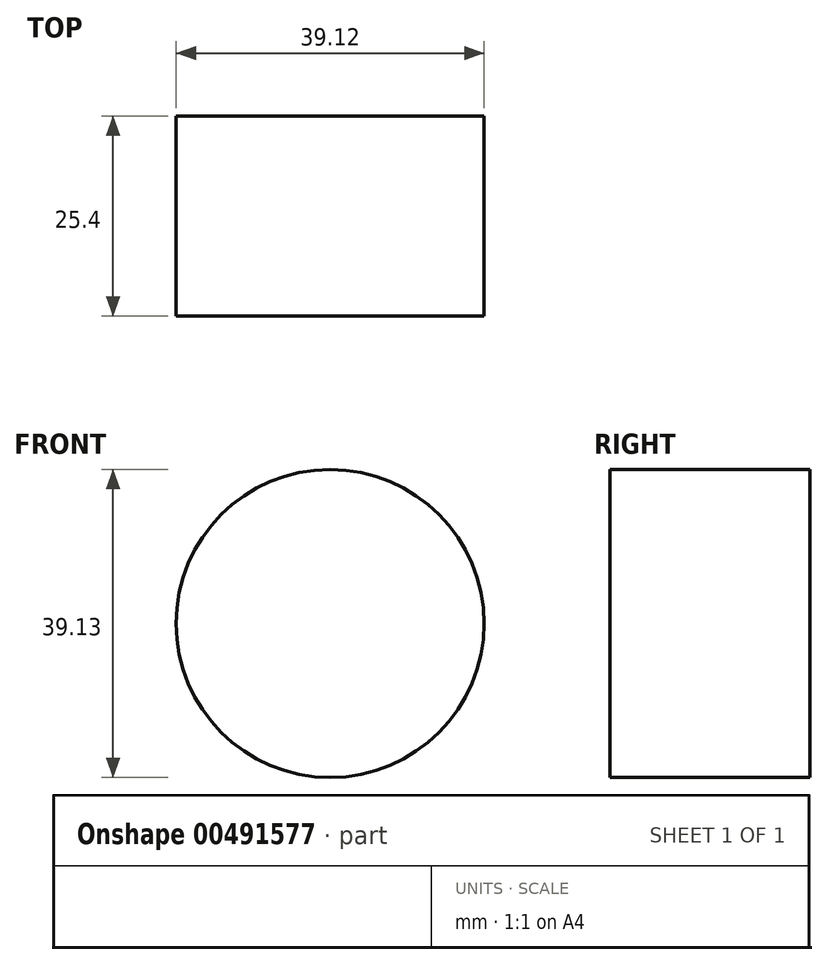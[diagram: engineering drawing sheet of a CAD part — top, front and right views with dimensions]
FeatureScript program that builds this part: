
annotation { "Feature Type Name" : "Feature", "Feature Type Description" : "" }
export const myFeature = defineFeature(function(context is Context, id is Id, definition is map)
    precondition{}
    {
        {
            var Q0;
            Q0=qCreatedBy(makeId("Front.planeOp"),FACE);
            var sketch = newSketch(context, id + "F0", { "sketchPlane" : qUnion([Q0])});
            skCircle(sketch, "E0", {"center": v(-71.06, 62.44) * mm, "radius": 19.56 * mm});
            skCircle(sketch, "E1", {"center": v(24.3, 42.07) * mm, "radius": 15.82 * mm});
            skCircle(sketch, "E2", {"center": v(-78.75, -35.84) * mm, "radius": 21.62 * mm});
            skCircle(sketch, "E3", {"center": v(80.62, -39.58) * mm, "radius": 32.86 * mm});
            skLineSegment(sketch, "E4", {"start": v(-128.2, 70.75) * mm, "end": v(-128.2, -20.88) * mm});
            skLineSegment(sketch, "E5", {"start": v(-128.2, -20.88) * mm, "end": v(-88.51, -99.63) * mm});
            skSolve(sketch);
        }
        {
            var Q0;
            Q0=makeQuery(id+"F0.imprint","IMPRINT",FACE,{"disambiguationData":[TD([[makeQuery(id+"F0.imprint","IMPRINT",EDGE,{"derivedFrom":sQuery(id+"F0.wireOp",EDGE,"E0")}),1.0]])]});
            extrude(context, id + "F1", {"entities" : qUnion([Q0]), "depth" : 25.4 * mm});
        }
    });
